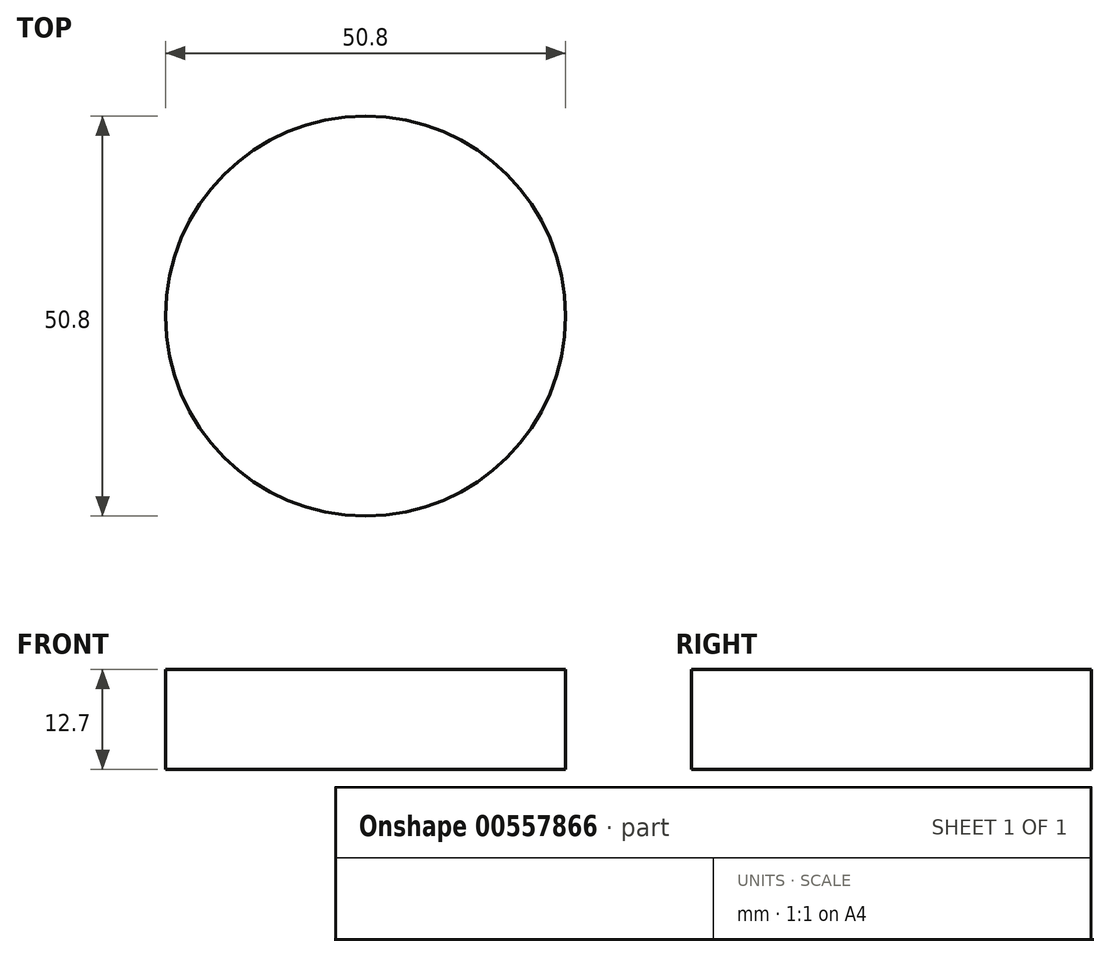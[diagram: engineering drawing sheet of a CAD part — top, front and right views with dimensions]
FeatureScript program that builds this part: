
annotation { "Feature Type Name" : "Feature", "Feature Type Description" : "" }
export const myFeature = defineFeature(function(context is Context, id is Id, definition is map)
    precondition{}
    {
        {
            var Q0;
            Q0=qCreatedBy(makeId("Top.planeOp"),FACE);
            var sketch = newSketch(context, id + "F0", { "sketchPlane" : qUnion([Q0])});
            skCircle(sketch, "E0", {"center": v(0, 0) * mm, "radius": 25.4 * mm});
            skSolve(sketch);
        }
        {
            var Q0;
            Q0 = qSketchRegion(id + "F0", true);
            extrude(context, id + "F1", {"entities" : qUnion([Q0]), "depth" : 12.7 * mm, "offsetDistance" : 25.4 * mm});
        }
    });
